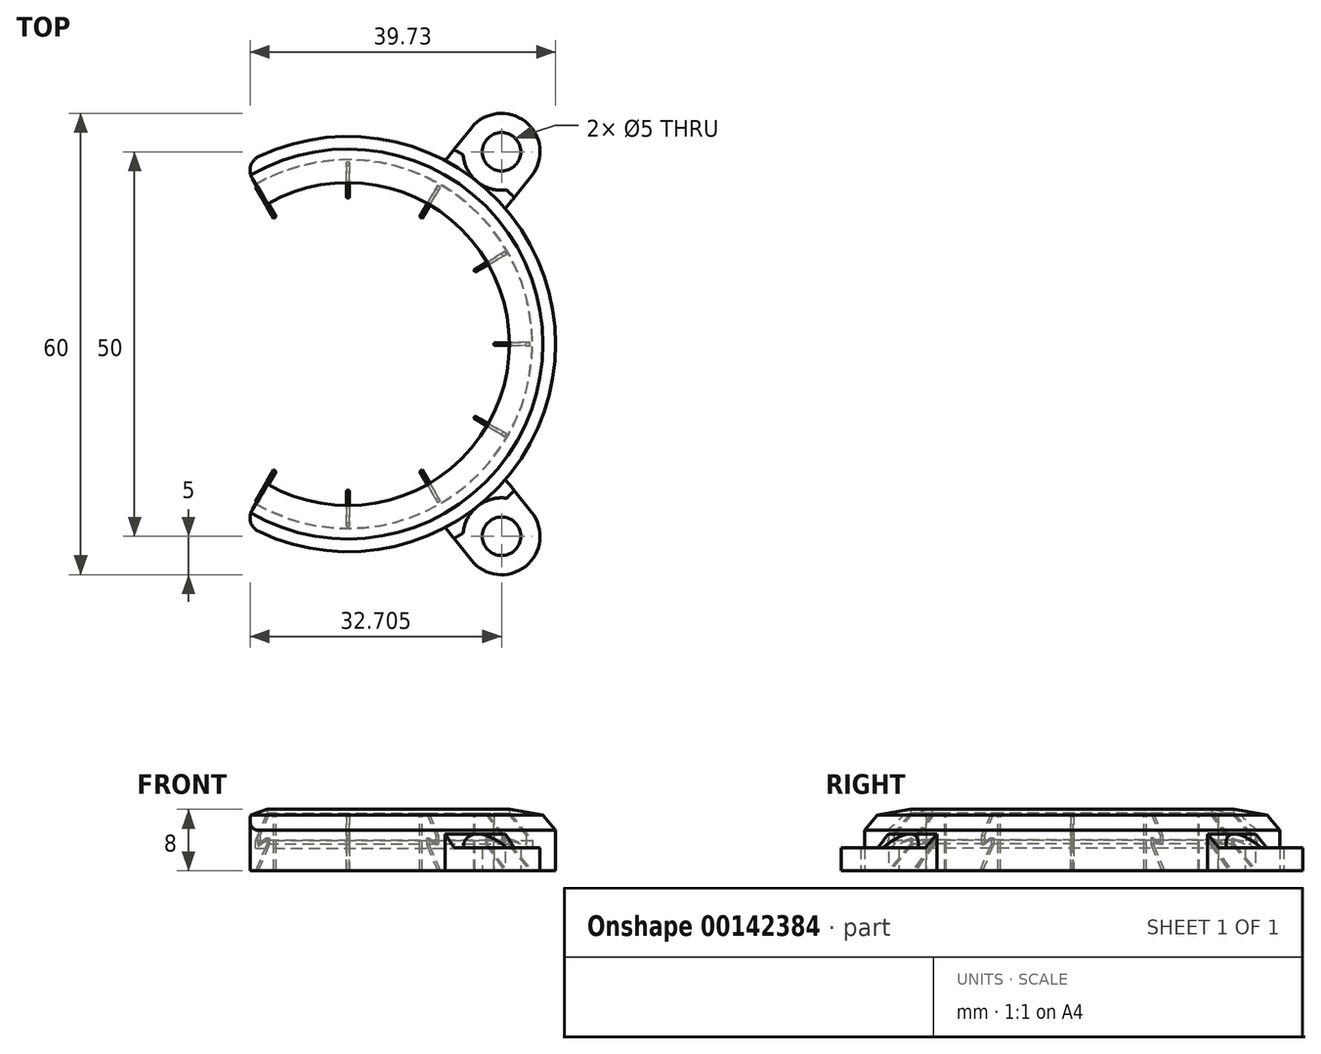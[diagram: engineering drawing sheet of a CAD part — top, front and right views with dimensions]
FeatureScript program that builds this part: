
annotation { "Feature Type Name" : "Feature", "Feature Type Description" : "" }
export const myFeature = defineFeature(function(context is Context, id is Id, definition is map)
    precondition{}
    {
        {
            var Q0;
            Q0=qCreatedBy(makeId("Front.planeOp"),FACE);
            var sketch = newSketch(context, id + "F0", { "sketchPlane" : qUnion([Q0])});
            skLineSegment(sketch, "E0", {"start": v(24, -0.08) * mm, "end": v(24, 0) * mm});
            skLineSegment(sketch, "E1", {"start": v(24, 2.9) * mm, "end": v(24, 3.92) * mm});
            skLineSegment(sketch, "E2", {"start": v(21, 8) * mm, "end": v(27, 6.94) * mm});
            skLineSegment(sketch, "E3", {"start": v(27, 6.94) * mm, "end": v(27, 0) * mm});
            skLineSegment(sketch, "E4", {"start": v(27, 0) * mm, "end": v(24, 0) * mm});
            skLineSegment(sketch, "E5", {"start": v(0, 0) * mm, "end": v(0, 81.93) * mm, "construction": true});
            skLineSegment(sketch, "E6", {"start": v(21, 4) * mm, "end": v(24, 2.9) * mm});
            skLineSegment(sketch, "E7", {"start": v(21, 26.97) * mm, "end": v(21, 0) * mm, "construction": true});
            skLineSegment(sketch, "E8", {"start": v(21, 8) * mm, "end": v(21, 7.5) * mm});
            skLineSegment(sketch, "E9", {"start": v(21, 7.5) * mm, "end": v(24, 3.92) * mm});
            skLineSegment(sketch, "E10", {"start": v(21, 4) * mm, "end": v(21, 3.5) * mm});
            skLineSegment(sketch, "E11", {"start": v(21, 3.5) * mm, "end": v(24, -0.08) * mm});
            skLineSegment(sketch, "E12", {"start": v(21, 0) * mm, "end": v(33.64, 0) * mm});
            skSolve(sketch);
        }
        {
            var Q0;
            Q0=makeQuery(id+"F0.imprint","IMPRINT",FACE,{"disambiguationData":[TD([[makeQuery(id+"F0.imprint","IMPRINT",EDGE,{"derivedFrom":sQuery(id+"F0.wireOp",EDGE,"E1")}),-1.0]])]});
            var Q1;
            Q1=sQuery(id+"F0.wireOp",EDGE,"E5");
            revolve(context, id + "F1", {"entities" : qUnion([Q0]), "axis" : qUnion([Q1]), "revolveType" : RevolveType.ONE_DIRECTION, "angle" : 120 * degree});
        }
        {
            var Q0;
            Q0=qCreatedBy(makeId("Top.planeOp"),FACE);
            var sketch = newSketch(context, id + "F2", { "sketchPlane" : qUnion([Q0])});
            skLineSegment(sketch, "E13", {"start": v(0, 0) * mm, "end": v(0, 16.68) * mm, "construction": true});
            skCircle(sketch, "E14", {"center": v(19.97, 25) * mm, "radius": 2.5 * mm});
            skLineSegment(sketch, "E15.bottom", {"start": v(12.66, 23.85) * mm, "end": v(20.47, 17.6) * mm});
            skLineSegment(sketch, "E15.top", {"start": v(19.19, 32.03) * mm, "end": v(27, 25.79) * mm});
            skLineSegment(sketch, "E15.left", {"start": v(12.66, 23.85) * mm, "end": v(19.19, 32.03) * mm});
            skLineSegment(sketch, "E15.right", {"start": v(20.47, 17.6) * mm, "end": v(27, 25.79) * mm});
            skLineSegment(sketch, "E16", {"start": v(19.97, 25) * mm, "end": v(23.1, 28.9) * mm, "construction": true});
            skSolve(sketch);
        }
        {
            var Q0;
            Q0=makeQuery(id+"F2.imprint","IMPRINT",FACE,{"disambiguationData":[TD([[makeQuery(id+"F2.imprint","IMPRINT",EDGE,{"derivedFrom":sQuery(id+"F2.wireOp",EDGE,"E14")}),-1.0]])]});
            extrude(context, id + "F3", {"entities" : qUnion([Q0]), "operationType" : NewBodyOperationType.ADD, "depth" : 3 * mm});
        }
        {
            var Q0;
            Q0=makeQuery(id+"F3.opExtrude","SWEPT_EDGE",EDGE,{"disambiguationData":[OSD([sQuery(id+"F2.wireOp",EDGE,"E15.top"),sQuery(id+"F2.wireOp",EDGE,"E15.left")])]});
            var Q1;
            Q1=makeQuery(id+"F3.opExtrude","SWEPT_EDGE",EDGE,{"disambiguationData":[OSD([sQuery(id+"F2.wireOp",EDGE,"E15.bottom"),sQuery(id+"F2.wireOp",EDGE,"E15.left")])]});
            var Q2;
            Q2=makeQuery(id+"F3.opExtrude","SWEPT_EDGE",EDGE,{"disambiguationData":[OSD([sQuery(id+"F2.wireOp",EDGE,"E15.bottom"),sQuery(id+"F2.wireOp",EDGE,"E15.right")])]});
            var Q3;
            Q3=makeQuery(id+"F3.opExtrude","SWEPT_EDGE",EDGE,{"disambiguationData":[OSD([sQuery(id+"F2.wireOp",EDGE,"E15.top"),sQuery(id+"F2.wireOp",EDGE,"E15.right")])]});
            fillet(context, id + "F4", {"entities" : qUnion([Q0, Q1, Q2, Q3]), "radius" : 5 * mm, "tangentPropagation" : true, "allowEdgeOverflow" : false});
        }
        {
            var Q0;
            Q0=makeQuery(id+"F1.opRevolve","SWEPT_EDGE",EDGE,{"disambiguationData":[OSD([sQuery(id+"F0.wireOp",EDGE,"E2"),sQuery(id+"F0.wireOp",EDGE,"E3")])]});
            chamfer(context, id + "F5", {"entities" : qUnion([Q0]), "width" : 2 * mm, "tangentPropagation" : true});
        }
        {
            var Q0;
            Q0=makeQuery(id+"F3.boolean.opBoolean","INTERSECT",EDGE,{"derivedFrom":[makeQuery(id+"F1.opRevolve","SWEPT_FACE",FACE,{"disambiguationData":[OSD([sQuery(id+"F0.wireOp",EDGE,"E3")])]}),makeQuery(id+"F3.opExtrude","CAP_FACE",FACE,{"disambiguationData":[OSD([sQuery(id+"F2.wireOp",EDGE,"E14"),sQuery(id+"F2.wireOp",EDGE,"E15.bottom"),sQuery(id+"F2.wireOp",EDGE,"E15.top"),sQuery(id+"F2.wireOp",EDGE,"E15.left"),sQuery(id+"F2.wireOp",EDGE,"E15.right")])],"isStart":false})]});
            chamfer(context, id + "F6", {"entities" : qUnion([Q0]), "width" : 1.8 * mm, "tangentPropagation" : true});
        }
        {
            var Q0;
            Q0=makeQuery(id+"F1.opRevolve","CAP_EDGE",EDGE,{"disambiguationData":[OSD([sQuery(id+"F0.wireOp",EDGE,"E3")])],"isStart":false});
            fillet(context, id + "F7", {"entities" : qUnion([Q0]), "radius" : 2 * mm, "tangentPropagation" : true, "allowEdgeOverflow" : false});
        }
        {
            var Q0;
            Q0=makeQuery(id+"F3.opExtrude","CAP_FACE",FACE,{"disambiguationData":[OSD([sQuery(id+"F2.wireOp",EDGE,"E14"),sQuery(id+"F2.wireOp",EDGE,"E15.bottom"),sQuery(id+"F2.wireOp",EDGE,"E15.top"),sQuery(id+"F2.wireOp",EDGE,"E15.left"),sQuery(id+"F2.wireOp",EDGE,"E15.right")])],"isStart":false});
            var sketch = newSketch(context, id + "F8", { "sketchPlane" : qUnion([Q0])});
            skCircle(sketch, "E17", {"center": v(19.97, 25) * mm, "radius": 5 * mm});
            skSolve(sketch);
        }
        {
            var Q0;
            Q0 = qSketchRegion(id + "F8", true);
            extrude(context, id + "F9", {"entities" : qUnion([Q0]), "operationType" : NewBodyOperationType.REMOVE, "endBound" : BoundingType.THROUGH_ALL, "depth" : 25 * mm});
        }
        {
            var Q0;
            Q0=qCreatedBy(makeId("Front.planeOp"),FACE);
            var sketch = newSketch(context, id + "F10", { "sketchPlane" : qUnion([Q0])});
            skLineSegment(sketch, "E18.0", {"start": v(20.8, 4.29) * mm, "end": v(23.2, 3.41) * mm});
            skLineSegment(sketch, "E18.1", {"start": v(20.8, 4.29) * mm, "end": v(20.8, 3.43) * mm});
            skLineSegment(sketch, "E18.2", {"start": v(20.8, 3.43) * mm, "end": v(23.68, 0) * mm});
            skLineSegment(sketch, "E19", {"start": v(23.2, 4.57) * mm, "end": v(23.2, 3.41) * mm});
            skLineSegment(sketch, "E20.0", {"start": v(20.74, 7.5) * mm, "end": v(23.2, 4.57) * mm});
            skLineSegment(sketch, "E21", {"start": v(23.68, 0) * mm, "end": v(19, 0) * mm});
            skLineSegment(sketch, "E22", {"start": v(19, 0) * mm, "end": v(19, 7.5) * mm});
            skLineSegment(sketch, "E23", {"start": v(19, 7.5) * mm, "end": v(20.74, 7.5) * mm});
            skSolve(sketch);
        }
        {
            var Q0;
            Q0 = qSketchRegion(id + "F10", true);
            var Q1;
            Q1=sQuery(id+"F0.wireOp",EDGE,"E5");
            revolve(context, id + "F11", {"entities" : qUnion([Q0]), "axis" : qUnion([Q1]), "revolveType" : RevolveType.SYMMETRIC, "angle" : 1 * degree});
        }
        {
            var Q0;
            Q0=makeQuery(id+"F11.opRevolve","SWEPT_BODY",BODY,{"disambiguationData":[OSD([sQuery(id+"F10.wireOp",EDGE,"E18.0"),sQuery(id+"F10.wireOp",EDGE,"E18.1"),sQuery(id+"F10.wireOp",EDGE,"E18.2"),sQuery(id+"F10.wireOp",EDGE,"E19"),sQuery(id+"F10.wireOp",EDGE,"E20.0"),sQuery(id+"F10.wireOp",EDGE,"E21"),sQuery(id+"F10.wireOp",EDGE,"E22"),sQuery(id+"F10.wireOp",EDGE,"E23")])]});
            var Q1;
            Q1=sQuery(id+"F0.wireOp",EDGE,"E5");
            circularPattern(context, id + "F12", {"entities" : qUnion([Q0]), "axis" : qUnion([Q1]), "angle" : 30 * degree, "instanceCount" : 5});
        }
        {
            var Q0;
            Q0=makeQuery(id+"F1.opRevolve","SWEPT_BODY",BODY,{"disambiguationData":[OSD([sQuery(id+"F0.wireOp",EDGE,"E0"),sQuery(id+"F0.wireOp",EDGE,"E1"),sQuery(id+"F0.wireOp",EDGE,"E2"),sQuery(id+"F0.wireOp",EDGE,"E3"),sQuery(id+"F0.wireOp",EDGE,"E4"),sQuery(id+"F0.wireOp",EDGE,"E6"),sQuery(id+"F0.wireOp",EDGE,"E8"),sQuery(id+"F0.wireOp",EDGE,"E9"),sQuery(id+"F0.wireOp",EDGE,"E10"),sQuery(id+"F0.wireOp",EDGE,"E11")])]});
            var Q1;
            Q1=makeQuery(id+"F11.opRevolve","SWEPT_BODY",BODY,{"disambiguationData":[OSD([sQuery(id+"F10.wireOp",EDGE,"E18.0"),sQuery(id+"F10.wireOp",EDGE,"E18.1"),sQuery(id+"F10.wireOp",EDGE,"E18.2"),sQuery(id+"F10.wireOp",EDGE,"E19"),sQuery(id+"F10.wireOp",EDGE,"E20.0"),sQuery(id+"F10.wireOp",EDGE,"E21"),sQuery(id+"F10.wireOp",EDGE,"E22"),sQuery(id+"F10.wireOp",EDGE,"E23")])]});
            var Q2;
            Q2=makeQuery(id+"F12.opPattern","COPY",BODY,{"derivedFrom":makeQuery(id+"F11.opRevolve","SWEPT_BODY",BODY,{"disambiguationData":[OSD([sQuery(id+"F10.wireOp",EDGE,"E18.0"),sQuery(id+"F10.wireOp",EDGE,"E18.1"),sQuery(id+"F10.wireOp",EDGE,"E18.2"),sQuery(id+"F10.wireOp",EDGE,"E19"),sQuery(id+"F10.wireOp",EDGE,"E20.0"),sQuery(id+"F10.wireOp",EDGE,"E21"),sQuery(id+"F10.wireOp",EDGE,"E22"),sQuery(id+"F10.wireOp",EDGE,"E23")])]}),"instanceName":"1"});
            var Q3;
            Q3=makeQuery(id+"F12.opPattern","COPY",BODY,{"derivedFrom":makeQuery(id+"F11.opRevolve","SWEPT_BODY",BODY,{"disambiguationData":[OSD([sQuery(id+"F10.wireOp",EDGE,"E18.0"),sQuery(id+"F10.wireOp",EDGE,"E18.1"),sQuery(id+"F10.wireOp",EDGE,"E18.2"),sQuery(id+"F10.wireOp",EDGE,"E19"),sQuery(id+"F10.wireOp",EDGE,"E20.0"),sQuery(id+"F10.wireOp",EDGE,"E21"),sQuery(id+"F10.wireOp",EDGE,"E22"),sQuery(id+"F10.wireOp",EDGE,"E23")])]}),"instanceName":"2"});
            var Q4;
            Q4=makeQuery(id+"F12.opPattern","COPY",BODY,{"derivedFrom":makeQuery(id+"F11.opRevolve","SWEPT_BODY",BODY,{"disambiguationData":[OSD([sQuery(id+"F10.wireOp",EDGE,"E18.0"),sQuery(id+"F10.wireOp",EDGE,"E18.1"),sQuery(id+"F10.wireOp",EDGE,"E18.2"),sQuery(id+"F10.wireOp",EDGE,"E19"),sQuery(id+"F10.wireOp",EDGE,"E20.0"),sQuery(id+"F10.wireOp",EDGE,"E21"),sQuery(id+"F10.wireOp",EDGE,"E22"),sQuery(id+"F10.wireOp",EDGE,"E23")])]}),"instanceName":"3"});
            var Q5;
            Q5=makeQuery(id+"F12.opPattern","COPY",BODY,{"derivedFrom":makeQuery(id+"F11.opRevolve","SWEPT_BODY",BODY,{"disambiguationData":[OSD([sQuery(id+"F10.wireOp",EDGE,"E18.0"),sQuery(id+"F10.wireOp",EDGE,"E18.1"),sQuery(id+"F10.wireOp",EDGE,"E18.2"),sQuery(id+"F10.wireOp",EDGE,"E19"),sQuery(id+"F10.wireOp",EDGE,"E20.0"),sQuery(id+"F10.wireOp",EDGE,"E21"),sQuery(id+"F10.wireOp",EDGE,"E22"),sQuery(id+"F10.wireOp",EDGE,"E23")])]}),"instanceName":"4"});
            var Q6;
            Q6=qCreatedBy(makeId("Front.planeOp"),FACE);
            mirror(context, id + "F13", {"operationType" : NewBodyOperationType.ADD, "entities" : qUnion([Q0, Q1, Q2, Q3, Q4, Q5]), "mirrorPlane" : qUnion([Q6])});
        }
    });
